# Revit family: Central algorítmica_Aguilera Electronica
name_source: partatom
category: Equipos eléctricos
revit_build: Autodesk Revit 2017 (Build: 20160225_1515(x64)
units: mm (PartAtom-declared; Revit-internal decimal feet)

## family parameters
Anfitrión = Cara
Compartido = No
Configuración de panel = Una columna
Corte con vacíos al cargar = No
Cota de conector redondo = Diámetro de uso
Número OmniClass = 23.85.30.21.11.14
Punto de cálculo de habitación = No
Tipo de pieza = Cuadro de control
Título OmniClass = Alarm Panels

## types (3) — shared parameters
Diámetro tubo = 20 mm  [stored 0.0656168 ft]
Elevación por defecto = 1200 mm
Fabricante = Aguilera Electrónica
Potencial eléctrico = 230 V
Símbolo = Sí
Símbolo texto modelo = Sí
URL = http://aguilera.es

## per-type parameters (varying)
| type | Alto | Ancho | Comentarios de tipo | Código de montaje | Descripción | Fondo | Modelo | Potencia aparente |
| Central algorítmica de 1 bucle | 274 mm  [stored 0.89895 ft] | 322 mm  [stored 1.05643 ft] | • Dispone de 1 bucle de 125 equipos, al que se conectan los detectores, pulsadores, módulos de control
de maniobras, y demás elementos que configuran la instalación.
• Fuente de alimentación conmutada de 27.2 Vcc 2 A. Cargador de baterías de emergencia.
• Capacidad para dos baterías de 12V / 7 Ah. Medidas: Alto 274 - Ancho 322 – Fondo 123 mm | D5030700 | Central inteligente de control de incendios con capacidad para 1 bucle de 125 equipos, al que se conectan los detectores, pulsadores, módulos de maniobras, de control y demás elementos que configuran la instalación.
Fuente de alimentación conmutada de 27.2 Vcc 2 A.
Cargador de baterías de emergencia.
Capacidad para alojar dos baterías de 12V / 7 Ah.
Medidas: Alto 274 - Ancho 322 Fondo 123 mm | 123 mm  [stored 0.403543 ft] | AE/SA-C1 | 460 VA |
| Central algorítmica de 2 bucles | 410 mm  [stored 1.34514 ft] | 310 mm  [stored 1.01706 ft] | • Provista de una tarjeta AE/SA-CTL de 2 blucles de 125 equipos cada uno, a los que se conectan los detectores,
pulsadores, módulos de maniobras, de control y demás elementos que configuran la instalación. Capacidad
de control de hasta 250 equipos.
• Fuente de alimentación conmutada de 27.2 Vcc 4 A. Cargador de baterías de emergencia.
• Capacidad para dos baterías de 12V / 7 Ah. Medidas: Alto 410 – Ancho 310 - Fondo 120 mm |  | Central inteligente de control de incendios con capacidad para una tarjeta AE/SA-CTL de 2 blucles de 125 equipos cada uno, a los que se conectan los detectores, pulsadores, módulos de maniobras, de control y demás elementos que configuran la instalación. Capacidad de control de 250 equipos.
Fuente de alimentación conmutada de 27.2 Vcc 4 A.
Cargador de baterías de emergencia.
Capacidad para alojar en su interior dos baterías de 12V / 7 Ah.
Medidas: Alto 410 Ancho 310 - Fondo 120 mm. | 120 mm  [stored 0.393701 ft] | AE/SA-C2 | 920 VA |
| Central algorítmica de 8 bucles | 500 mm  [stored 1.64042 ft] | 390 mm  [stored 1.27953 ft] | Central inteligente de control de incendios con bus para la conexión de 1 a 4 tarjetas AE/SA-CTL. Cada tarjeta
controla dos bucles algorítmicos bidireccionales, con capacidad de 125 equipos cada uno, a los que se
conectan los detectores, pulsadores, módulos de maniobras, de control y demás elementos que configuran
la instalación.
• Capacidad de control de hasta 1000 equipos, que dependiendo del tipo puede significar el control de más
de 3000 puntos independientes. Para cada 250 equipos la central dispone de un microprocesador independiente.
• Fuente de alimentación conmutada independiente de 27,2 Vcc 4 A.
• Cargador de baterías de emergencia. Capacidad para dos baterías de 12V / 17 Ah.
• Medidas: Alto 500 – Ancho 390 – Fondo 145 mm |  | Central inteligente de control de incendios con bus para la conexión de 1 a 4 tarjetas AE/SA-CTL. Cada tarjeta controla dos bucles algorítmicos bidireccionales, con capacidad de 125 equipos cada uno, a los que se conectan los detectores, pulsadores, módulos de maniobras, de control y demás elementos que configuran la instalación.
La capacidad de control de la central se eleva a 1000 equipos, que dependiendo del tipo puede significar el control de más de 3000 puntos independientes. Para cada 250 equipos la central dispone de un microprocesador independiente. Fuente de alimentación conmutada independiente de 27,2 Vcc 4 A.
Cargador de baterías de emergencia. La central dispone de capacidad para alojar en su interior dos baterías de 12V / 17 Ah.
Medidas: Alto 500 Ancho 390 Fondo 145 mm
Incluye Tarjeta de bucles. | 145 mm  [stored 0.475722 ft] | AE/SA-C8 | 920 VA |

note: [stored X ft] marks values corroborated as IEEE doubles in the binary element streams (Revit-internal decimal feet)
